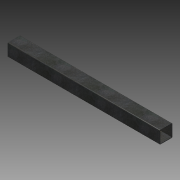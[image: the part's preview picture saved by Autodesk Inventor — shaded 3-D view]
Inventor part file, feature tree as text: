
AUTODESK INVENTOR PART (.ipt)
format: ipt  version: 2015 SP1 (Build 190203100, 203)  size: 92,672 bytes
history: native  units: in
note: dims shown in document units (in); Inventor stores cm internally (conversion verified against a paired STEP export)
features: extrude x1, fillet x1, sketch x1
ambient origin geometry x8: Origin, YZ Plane, XZ Plane, XY Plane, X Axis, Y Axis, Z Axis, Center Point
bodies: Solid1 (feature_tree)
feature tree (3):
  extrude  "Extrusion1"  Depth=2.0in
  fillet  "Fillet1"  Radius=0.083in
  sketch  "Sketch1"  dims[d0=2.0in d1=2.0in d2=0.083in d3=24.0in d4=0.0in d5=0.125in]
